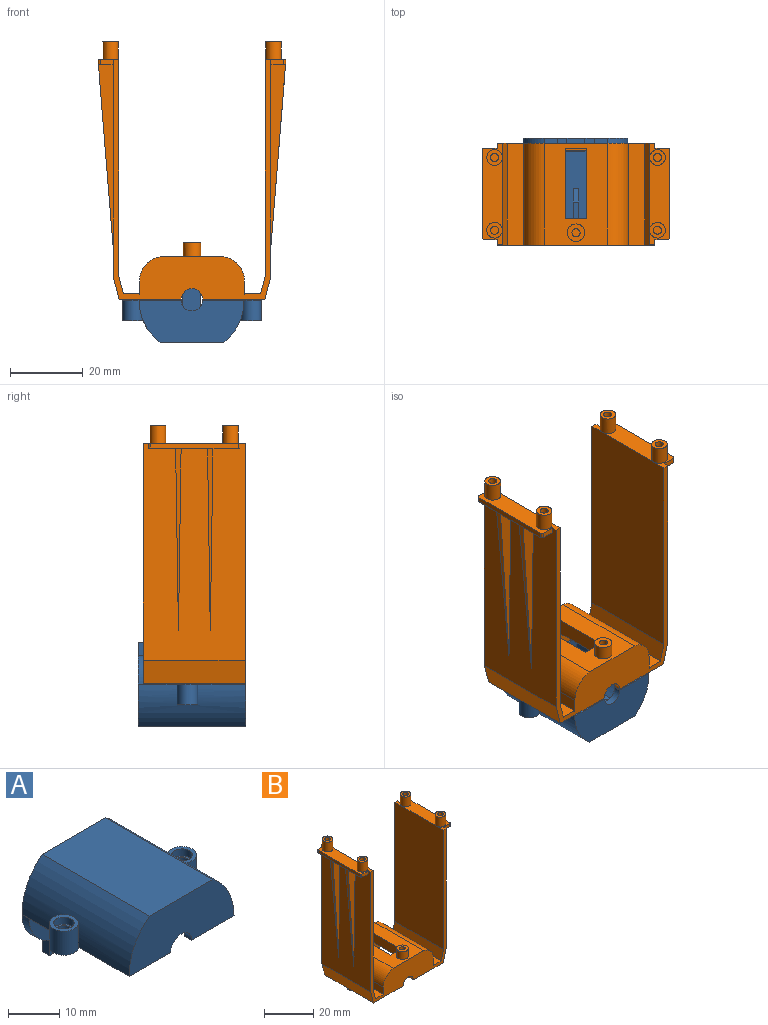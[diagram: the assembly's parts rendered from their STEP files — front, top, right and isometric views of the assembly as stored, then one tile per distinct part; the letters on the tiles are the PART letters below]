
ASSEMBLY  parts=2 mates=1
PART A: 76 faces, bbox 38.1x29.5x23.1 mm
  f0: plane 3.71x2mm, normal (-1,0,0), area 7.4mm2, adj f1,f3,f4,f74
  f1: plane 3.69x2mm, normal (0,0,-1), area 7.4mm2, adj f0,f3,f4,f60
  f2: cylinder r=14.66mm len=2mm, axis (0,1,0), area 0mm2, adj f4,f6,f13,f73
  f3: plane 11.58x9.24mm, normal (0,-1,0), area 74.7mm2, adj f0,f1,f10,f11,f60,f74
  f4: plane 28.86x23.15mm, normal (0,1,0), area 453.5mm2, adj f0,f1,f2,f6,f7,f11,f12,f14
  f5: plane 5.97x4.94mm, normal (0,-1,0), area 25mm2, adj f14,f61,f62,f72
  f6: plane 3.67x2mm, normal (0,0,-1), area 7.3mm2, adj f2,f4,f13,f63
  f7: plane 4.94x2mm, normal (0,0,-1), area 9.9mm2, adj f4,f9,f61,f62
  f8: plane 9.57x7.24mm, normal (0,-1,0), area 57.2mm2, adj f10,f14,f30,f60
  f9: plane 16.48x4.94mm, normal (0,-1,0), area 79.5mm2, adj f7,f61,f62,f72
  f10: plane 27.5x16.13mm, normal (0,0,-1), area 94.6mm2, adj f3,f8,f20,f23,f25,f28,f29,f30
  f11: cylinder r=14.66mm len=2mm, axis (0,1,0), area 0.1mm2, adj f3,f4,f28,f74
  f12: cylinder r=14.66mm len=2mm, axis (0,1,0), area 0.1mm2, adj f4,f13,f15,f75
  f13: plane 11.58x9.5mm, normal (0,-1,0), area 76.2mm2, adj f2,f6,f12,f26,f63,f73,f75
  f14: plane 27.5x16.11mm, normal (0,0,-1), area 316.2mm2, adj f4,f5,f8,f16,f18,f19,f20,f30
  f15: cylinder r=14.23mm len=29.5mm, axis (0,-1,0), area 375.1mm2, adj f4,f12,f26,f27,f29,f35
  f16: cylinder r=12.23mm len=24mm, axis (0,-1,0), area 252.2mm2, adj f14,f20,f26,f31,f55,f56,f57
  f17: plane 10x1.5mm, normal (0,0,-1), area 15mm2, adj f18,f19,f20,f46
  f18: plane 13.83x2mm, normal (1,0,0), area 23.8mm2, adj f14,f17,f20,f46
  f19: plane 13.83x2mm, normal (-1,0,0), area 23.8mm2, adj f14,f17,f20,f46
  f20: plane 24.86x9.57mm, normal (0,1,0), area 196.4mm2, adj f10,f14,f16,f17,f18,f19,f26,f30
  f21: cylinder r=14.23mm len=0.96mm, axis (0,-1,0), area 0.2mm2, adj f22,f42
  f22: cylinder r=2mm len=4mm, axis (0,0,-1), area 22.4mm2, adj f21,f37,f42,f44
  f23: cylinder r=2mm len=5.71mm, axis (0,0,-1), area 47.2mm2, adj f10,f25,f34,f38,f40,f41
  f24: cylinder r=14.23mm len=2.18mm, axis (0,-1,0), area 4.1mm2, adj f26,f36,f45
  f25: cylinder r=14.23mm len=1.62mm, axis (0,-1,0), area 1.3mm2, adj f10,f23
  f26: plane 27.5x16.13mm, normal (0,0,-1), area 94.8mm2, adj f13,f15,f16,f20,f24,f29,f31,f32
  f27: plane 29.5x17.5mm, normal (0,0,1), area 516.2mm2, adj f4,f15,f28,f29
  f28: cylinder r=14.23mm len=29.5mm, axis (0,-1,0), area 374.9mm2, adj f4,f10,f11,f27,f29,f33
  f29: plane 28.86x11.57mm, normal (0,-1,0), area 281.5mm2, adj f10,f15,f26,f27,f28,f32
  f30: cylinder r=12.23mm len=24mm, axis (0,-1,0), area 249.7mm2, adj f8,f10,f14,f20,f48,f49,f50
  f31: plane 9.57x7.5mm, normal (0,-1,0), area 58.8mm2, adj f14,f16,f26,f63
  f32: cylinder r=2.93mm len=5.86mm, axis (0,-1,0), area 18.4mm2, adj f10,f20,f26,f29
  f33: cylinder r=2.82mm len=5.71mm, axis (0,0,-1), area 82.1mm2, adj f10,f28,f34
  f34: plane 5.64x5.64mm, normal (0,0,1), area 12.4mm2, adj f23,f33
  f35: cylinder r=2.82mm len=5.71mm, axis (0,0,-1), area 77.7mm2, adj f15,f26,f37
  f36: cylinder r=2mm len=4mm, axis (0,0,-1), area 20.8mm2, adj f24,f26,f45
  f37: plane 5.64x5.64mm, normal (0,0,1), area 12.4mm2, adj f22,f35
  f38: plane 2x0.96mm, normal (1,0,0), area 1.9mm2, adj f23,f40,f41
  f39: cylinder r=1.5mm len=3mm, axis (0,0,-1), area 18.8mm2, adj f40,f41
  f40: plane 4x3.94mm, normal (0,0,1), area 5.5mm2, adj f23,f38,f39
  f41: plane 4x3.94mm, normal (0,0,-1), area 5.5mm2, adj f23,f38,f39
  f42: plane 1.18x0.96mm, normal (-1,0,0), area 1.1mm2, adj f21,f22,f44
  f43: cylinder r=1.5mm len=3mm, axis (0,0,-1), area 18.8mm2, adj f44,f45
  f44: plane 4x3.94mm, normal (0,0,1), area 5.5mm2, adj f22,f42,f43
  f45: plane 4x3.81mm, normal (0,0,-1), area 5.3mm2, adj f24,f36,f43
  f46: plane 3.83x2mm, normal (0,0.46,-0.89), area 6.5mm2, adj f14,f17,f18,f19
  f47: plane 2x1.5mm, normal (1,0,0), area 3mm2, adj f48,f49,f50,f53
  f48: plane 3.66x1.5mm, normal (0,0,-1), area 5.5mm2, adj f30,f47,f49,f50
  f49: plane 6.41x5.5mm, normal (0,-1,0), area 18.1mm2, adj f14,f30,f47,f48,f51,f52,f53
  f50: plane 6.41x5.5mm, normal (0,1,0), area 18.1mm2, adj f14,f30,f47,f48,f51,f52,f53
  f51: plane 2x1.5mm, normal (1,0,0), area 3mm2, adj f14,f49,f50,f52
  f52: plane 1.5x1.25mm, normal (0,0,-1), area 1.9mm2, adj f49,f50,f51,f53
  f53: cylinder r=1.5mm len=1.5mm, axis (0,-1,0), area 3.5mm2, adj f47,f49,f50,f52
  f54: plane 3.5x1.5mm, normal (-1,0,0), area 5.3mm2, adj f55,f56,f57,f59
  f55: plane 3.86x1.5mm, normal (0,0,-1), area 5.8mm2, adj f16,f54,f56,f57
  f56: plane 6.61x5.5mm, normal (0,-1,0), area 18.3mm2, adj f14,f16,f54,f55,f58,f59
  f57: plane 6.61x5.5mm, normal (0,1,0), area 18.3mm2, adj f14,f16,f54,f55,f58,f59
  f58: plane 2x1.5mm, normal (-1,0,0), area 3mm2, adj f14,f56,f57,f59
  f59: plane 2.75x1.5mm, normal (0,0,-1), area 4.1mm2, adj f54,f56,f57,f58
  f60: plane 21.15x3.5mm, normal (1,0,0), area 56.6mm2, adj f1,f3,f4,f8,f10,f14
  f61: plane 21.15x3.5mm, normal (-1,0,0), area 51.2mm2, adj f4,f5,f7,f9,f14,f72
  f62: plane 21.15x3.5mm, normal (1,0,0), area 51.2mm2, adj f4,f5,f7,f9,f14,f72
  f63: plane 21.15x3.5mm, normal (-1,0,0), area 56.6mm2, adj f4,f6,f13,f14,f26,f31
  f64: cylinder r=2.17mm len=4.35mm, axis (0,0,1), area 6.8mm2, adj f14,f65
  f65: plane 4.35x4.35mm, normal (0,0,-1), area 14.9mm2, adj f64
  f66: cylinder r=2.17mm len=4.35mm, axis (0,0,1), area 6.8mm2, adj f14,f67
  f67: plane 4.35x4.35mm, normal (0,0,-1), area 14.9mm2, adj f66
  f68: cylinder r=2.17mm len=4.35mm, axis (0,0,1), area 6.8mm2, adj f14,f69
  f69: plane 4.35x4.35mm, normal (0,0,-1), area 14.9mm2, adj f68
  f70: cylinder r=2.17mm len=4.35mm, axis (0,0,1), area 6.8mm2, adj f14,f71
  f71: plane 4.35x4.35mm, normal (0,0,-1), area 14.9mm2, adj f70
  f72: cylinder r=3mm len=4.94mm, axis (0,-1,0), area 8.7mm2, adj f5,f9,f61,f62
  f73: plane 3.69x2mm, normal (1,0,0), area 7.4mm2, adj f2,f4,f13,f75
  f74: cylinder r=8.25mm len=7.82mm, axis (0,-1,0), area 20.5mm2, adj f0,f3,f4,f11
  f75: cylinder r=8.3mm len=7.82mm, axis (0,-1,0), area 20.8mm2, adj f4,f12,f13,f73
PART B: 131 faces, bbox 51.5x28x73.1 mm
  f0: plane 7.28x4.03mm, normal (0,0,-1), area 29.3mm2, adj f4,f6,f25,f102
  f1: plane 7.41x4.02mm, normal (0,0,-1), area 29.7mm2, adj f2,f5,f25,f66,f102
  f2: cylinder r=0.5mm len=1.5mm, axis (0,0,1), area 1.2mm2, adj f1,f3,f23,f66,f102
  f3: plane 24.1x1.5mm, normal (-1,0,0), area 33.9mm2, adj f2,f23,f24,f67,f102
  f4: plane 49.87x4.02mm, normal (0,-1,-0.01), area 100.2mm2, adj f0,f25,f102
  f5: plane 49.87x4.02mm, normal (0,1,-0.02), area 100.2mm2, adj f1,f25,f102
  f6: plane 50x4.03mm, normal (0,1,-0.01), area 100.7mm2, adj f0,f25,f102
  f7: plane 50x4.03mm, normal (0,1,-0.02), area 100.8mm2, adj f19,f22,f101
  f8: plane 7.41x4.02mm, normal (0,0,-1), area 29.7mm2, adj f11,f13,f19,f71,f101
  f9: plane 7.28x4.03mm, normal (0,0,-1), area 29.3mm2, adj f12,f14,f19,f101
  f10: plane 24.1x1.5mm, normal (1,0,0), area 33.9mm2, adj f11,f22,f47,f70,f101
  f11: cylinder r=0.5mm len=1.5mm, axis (0,0,1), area 1.2mm2, adj f8,f10,f47,f71,f101
  f12: plane 50x4.03mm, normal (0,-1,-0.01), area 100.7mm2, adj f9,f19,f101
  f13: plane 49.86x4.02mm, normal (0,-1,-0.01), area 100.2mm2, adj f8,f19,f101
  f14: plane 49.86x4.02mm, normal (0,1,-0.01), area 100.2mm2, adj f9,f19,f101
  f15: plane 24.86x9.68mm, normal (0,1,0), area 204.8mm2, adj f17,f28,f30,f35,f36,f37,f38,f39
  f16: plane 24.86x9.68mm, normal (0,-1,0), area 181.8mm2, adj f18,f28,f30,f35,f36,f37,f38,f39
  f17: plane 13.2x4.07mm, normal (0,0,-1), area 53.8mm2, adj f15,f35,f94,f97
  f18: plane 9.3x4.07mm, normal (0,0,-1), area 37.9mm2, adj f16,f35,f94,f96
  f19: plane 59.6x28mm, normal (1,0,0), area 1556.2mm2, adj f7,f8,f9,f12,f13,f14,f20,f21
  f20: plane 65.93x43.42mm, normal (0,1,0), area 505.3mm2, adj f19,f23,f25,f26,f27,f28,f29,f30
  f21: plane 65.93x43.42mm, normal (0,-1,0), area 516.2mm2, adj f19,f23,f25,f26,f27,f28,f29,f30
  f22: plane 7.41x4.03mm, normal (0,0,-1), area 29.8mm2, adj f7,f10,f19,f69,f70
  f23: plane 28x5.53mm, normal (0,0,1), area 113.9mm2, adj f2,f3,f20,f21,f25,f54,f66,f67
  f24: plane 7.41x4.03mm, normal (0,0,-1), area 29.8mm2, adj f3,f25,f67,f68,f88
  f25: plane 59.6x28mm, normal (-1,0,0), area 1556.2mm2, adj f0,f1,f4,f5,f6,f20,f21,f23
  f26: plane 28x17.5mm, normal (0,0,1), area 357.3mm2, adj f20,f21,f31,f32,f58,f62,f63,f64
  f27: plane 28x0.02mm, normal (0,0,1), area 0.5mm2, adj f20,f21,f33,f53
  f28: plane 28x17.09mm, normal (0,0,-1), area 205mm2, adj f15,f16,f20,f21,f40,f52,f118,f121
  f29: plane 28x0.02mm, normal (0,0,1), area 0.5mm2, adj f20,f21,f34,f51
  f30: plane 28x17.09mm, normal (0,0,-1), area 205mm2, adj f15,f16,f20,f21,f40,f46,f114,f125
  f31: cylinder r=6.77mm len=28mm, axis (0,-1,0), area 267.1mm2, adj f20,f21,f26,f34
  f32: cylinder r=6.77mm len=28mm, axis (0,-1,0), area 267.1mm2, adj f20,f21,f26,f33
  f33: plane 28x3.65mm, normal (-1,0,0), area 102.2mm2, adj f20,f21,f27,f32
  f34: plane 28x3.65mm, normal (1,0,0), area 102.2mm2, adj f20,f21,f29,f31
  f35: cylinder r=4.77mm len=24mm, axis (0,-1,0), area 150.3mm2, adj f15,f16,f17,f18,f39,f96,f97,f98
  f36: plane 24x4.07mm, normal (0,0,-1), area 97.8mm2, adj f15,f16,f37,f92
  f37: cylinder r=4.77mm len=24mm, axis (0,-1,0), area 150.3mm2, adj f15,f16,f36,f38,f107,f108,f110,f112
  f38: plane 24x6.5mm, normal (1,0,0), area 156mm2, adj f15,f16,f37,f121,f123,f124
  f39: plane 24x6.5mm, normal (-1,0,0), area 156mm2, adj f15,f16,f35,f125,f127,f128
  f40: cylinder r=2.93mm len=5.86mm, axis (0,-1,0), area 18.4mm2, adj f15,f21,f28,f30
  f41: plane 2x0.19mm, normal (-0.59,0,-0.81), area 0.5mm2, adj f16,f20,f45,f129
  f42: plane 2x0.19mm, normal (0.59,0,-0.81), area 0.5mm2, adj f16,f20,f43,f130
  f43: cylinder r=1mm len=2mm, axis (0,1,0), area 1.3mm2, adj f16,f20,f42,f44
  f44: plane 4.75x2mm, normal (0,0,-1), area 9.5mm2, adj f16,f20,f43,f45
  f45: cylinder r=1mm len=2mm, axis (0,1,0), area 1.3mm2, adj f16,f20,f41,f44
  f46: plane 28x6.33mm, normal (0.97,0,-0.26), area 183.4mm2, adj f19,f20,f21,f30
  f47: plane 28x5.53mm, normal (0,0,1), area 113.9mm2, adj f10,f11,f19,f20,f21,f48,f69,f70
  f48: plane 59.4x28mm, normal (-1,0,0), area 1663.3mm2, adj f20,f21,f47,f49
  f49: plane 28x5.03mm, normal (-0.97,0,0.26), area 145.6mm2, adj f20,f21,f48,f50
  f50: plane 28x4.42mm, normal (0,0,1), area 123.7mm2, adj f20,f21,f49,f51
  f51: plane 28x0.15mm, normal (-1,0,0), area 4.2mm2, adj f20,f21,f29,f50
  f52: plane 28x6.33mm, normal (-0.97,0,-0.26), area 183.4mm2, adj f20,f21,f25,f28
  f53: plane 28x0.15mm, normal (1,0,0), area 4.2mm2, adj f20,f21,f27,f55
  f54: plane 59.4x28mm, normal (1,0,0), area 1663.3mm2, adj f20,f21,f23,f56
  f55: plane 28x4.42mm, normal (0,0,1), area 123.7mm2, adj f20,f21,f53,f56
  f56: plane 28x5.03mm, normal (0.97,0,0.26), area 145.6mm2, adj f20,f21,f54,f55
  f57: cylinder r=1.11mm len=3.8mm, axis (0,0,-1), area 26.5mm2, adj f59,f60
  f58: cylinder r=2.4mm len=4.8mm, axis (0,0,-1), area 57.3mm2, adj f26,f59
  f59: plane 4.8x4.8mm, normal (0,0,1), area 14.2mm2, adj f57,f58
  f60: plane 2.22x2.22mm, normal (0,0,1), area 3.9mm2, adj f57
  f61: plane 6x0.5mm, normal (0,0,1), area 3mm2, adj f16,f62,f63,f64
  f62: plane 24.5x5mm, normal (1,0,0), area 96.6mm2, adj f15,f16,f26,f61,f64,f65,f93,f99
  f63: plane 24.5x5mm, normal (-1,0,0), area 96.6mm2, adj f15,f16,f26,f61,f64,f65,f95,f100
  f64: plane 6x5mm, normal (0,-1,0), area 30mm2, adj f26,f61,f62,f63
  f65: plane 6x4.48mm, normal (0,1,0), area 17.9mm2, adj f26,f62,f63,f89,f90,f91,f99,f100
  f66: plane 3.53x1.5mm, normal (0,1,0), area 5.3mm2, adj f1,f2,f23,f25
  f67: cylinder r=0.5mm len=1.5mm, axis (0,0,1), area 1.2mm2, adj f3,f23,f24,f68
  f68: plane 3.53x1.5mm, normal (0,-1,0), area 5.3mm2, adj f23,f24,f25,f67
  f69: plane 3.53x1.5mm, normal (0,1,0), area 5.3mm2, adj f19,f22,f47,f70
  f70: cylinder r=0.5mm len=1.5mm, axis (0,0,1), area 1.2mm2, adj f10,f22,f47,f69
  f71: plane 3.53x1.5mm, normal (0,-1,0), area 5.3mm2, adj f8,f11,f19,f47
  f72: cylinder r=1.11mm len=4.9mm, axis (0,0,-1), area 34.2mm2, adj f74,f75
  f73: cylinder r=2.15mm len=4.9mm, axis (0,0,-1), area 66.3mm2, adj f23,f74
  f74: plane 4.31x4.31mm, normal (0,0,1), area 10.7mm2, adj f72,f73
  f75: plane 2.22x2.22mm, normal (0,0,1), area 3.9mm2, adj f72
  f76: cylinder r=2.15mm len=4.9mm, axis (0,0,-1), area 66.3mm2, adj f23,f78
  f77: cylinder r=1.11mm len=4.9mm, axis (0,0,-1), area 34.2mm2, adj f78,f79
  f78: plane 4.31x4.31mm, normal (0,0,1), area 10.7mm2, adj f76,f77
  f79: plane 2.22x2.22mm, normal (0,0,1), area 3.9mm2, adj f77
  f80: cylinder r=1.11mm len=4.9mm, axis (0,0,-1), area 34.2mm2, adj f82,f83
  f81: cylinder r=2.15mm len=4.9mm, axis (0,0,-1), area 66.3mm2, adj f47,f82
  f82: plane 4.31x4.31mm, normal (0,0,1), area 10.7mm2, adj f80,f81
  f83: plane 2.22x2.22mm, normal (0,0,1), area 3.9mm2, adj f80
  f84: cylinder r=2.15mm len=4.9mm, axis (0,0,-1), area 66.3mm2, adj f47,f86
  f85: cylinder r=1.11mm len=4.9mm, axis (0,0,-1), area 34.2mm2, adj f86,f87
  f86: plane 4.31x4.31mm, normal (0,0,1), area 10.7mm2, adj f84,f85
  f87: plane 2.22x2.22mm, normal (0,0,1), area 3.9mm2, adj f85
  f88: plane 50x4.03mm, normal (0,-1,-0.01), area 100.8mm2, adj f24,f25,f102
  f89: plane 5.4x2mm, normal (-1,0,0), area 10.8mm2, adj f15,f65,f91,f99
  f90: plane 5.4x2mm, normal (1,0,0), area 10.8mm2, adj f15,f65,f91,f100
  f91: plane 5.4x1.5mm, normal (0,0,-1), area 8.1mm2, adj f15,f65,f89,f90
  f92: plane 24x2.48mm, normal (-1,0,0), area 57.3mm2, adj f15,f16,f36,f93,f107,f108,f109,f110
  f93: plane 24x1.5mm, normal (0,0,-1), area 36mm2, adj f15,f16,f62,f92
  f94: plane 24x2.48mm, normal (1,0,0), area 56.5mm2, adj f15,f16,f17,f18,f95,f96,f97,f105
  f95: plane 24x1.5mm, normal (0,0,-1), area 36mm2, adj f15,f16,f63,f94
  f96: plane 7.93x4.48mm, normal (0,1,0), area 25.7mm2, adj f18,f35,f94,f98,f103,f104,f105,f106
  f97: plane 7.93x4.48mm, normal (0,-1,0), area 25.7mm2, adj f17,f35,f94,f98,f103,f104,f105,f106
  f98: plane 1.5x0.48mm, normal (1,0,0), area 0.7mm2, adj f35,f96,f97,f103
  f99: plane 5.4x2.25mm, normal (0,0,-1), area 12.1mm2, adj f15,f62,f65,f89
  f100: plane 5.4x2.25mm, normal (0,0,-1), area 12.1mm2, adj f15,f63,f65,f90
  f101: plane 50.27x17.34mm, normal (1,0,-0.08), area 77.6mm2, adj f7,f8,f9,f10,f11,f12,f13,f14
  f102: plane 50.26x17.33mm, normal (-1,0,-0.08), area 77.5mm2, adj f0,f1,f2,f3,f4,f5,f6,f25
  f103: plane 1.5x1.32mm, normal (0,0,1), area 2mm2, adj f35,f96,f97,f98
  f104: plane 5.93x1.5mm, normal (0,0,-1), area 8.9mm2, adj f35,f96,f97,f106
  f105: plane 2x1.5mm, normal (0,0,-1), area 3mm2, adj f94,f96,f97,f106
  f106: plane 2.5x1.5mm, normal (-1,0,0), area 3.8mm2, adj f96,f97,f104,f105
  f107: plane 7.93x4mm, normal (0,-1,0), area 23.7mm2, adj f37,f92,f109,f110,f111,f112
  f108: plane 7.93x4mm, normal (0,1,0), area 23.7mm2, adj f37,f92,f109,f110,f111,f112
  f109: plane 2x1.5mm, normal (0,0,-1), area 3mm2, adj f92,f107,f108,f111
  f110: plane 5.42x1.5mm, normal (0,0,1), area 8.1mm2, adj f37,f92,f107,f108
  f111: plane 2.5x1.5mm, normal (1,0,0), area 3.8mm2, adj f107,f108,f109,f112
  f112: plane 5.93x1.5mm, normal (0,0,-1), area 8.9mm2, adj f37,f107,f108,f111
  f113: cylinder r=1.1mm len=2.29mm, axis (0,0,1), area 15.9mm2, adj f115,f116
  f114: cylinder r=2.15mm len=4.3mm, axis (0,0,1), area 30.9mm2, adj f30,f115
  f115: plane 4.3x4.3mm, normal (0,0,-1), area 10.7mm2, adj f113,f114
  f116: plane 2.21x2.21mm, normal (0,0,-1), area 3.8mm2, adj f113
  f117: cylinder r=1.1mm len=2.29mm, axis (0,0,1), area 15.9mm2, adj f119,f120
  f118: cylinder r=2.15mm len=4.3mm, axis (0,0,1), area 30.9mm2, adj f28,f119
  f119: plane 4.3x4.3mm, normal (0,0,-1), area 10.7mm2, adj f117,f118
  f120: plane 2.21x2.21mm, normal (0,0,-1), area 3.8mm2, adj f117
  f121: plane 1.5x1.14mm, normal (0,-1,0), area 1.7mm2, adj f28,f38,f122,f124
  f122: plane 24x1.5mm, normal (-1,0,0), area 36mm2, adj f28,f121,f123,f124
  f123: plane 1.5x1.14mm, normal (0,1,0), area 1.7mm2, adj f28,f38,f122,f124
  f124: plane 24x1.14mm, normal (0,0,-1), area 27.4mm2, adj f38,f121,f122,f123
  f125: plane 1.5x1.14mm, normal (0,1,0), area 1.7mm2, adj f30,f39,f126,f128
  f126: plane 24x1.5mm, normal (1,0,0), area 36mm2, adj f30,f125,f127,f128
  f127: plane 1.5x1.14mm, normal (0,-1,0), area 1.7mm2, adj f30,f39,f126,f128
  f128: plane 24x1.14mm, normal (0,0,-1), area 27.4mm2, adj f39,f125,f126,f127
  f129: cylinder r=4mm len=2.67mm, axis (0,-1,0), area 6.4mm2, adj f16,f20,f30,f41
  f130: cylinder r=4mm len=2.67mm, axis (0,-1,0), area 6.4mm2, adj f16,f20,f28,f42
PLACE A rot(axis=(0,1,0),180deg) t=(-0.74,-14.22,-33.88)mm
PLACE B t=(-0.73,-0.11,-33.59)mm
MATE fastened A.f23 <-> B.f113  axis (0,0,1) through (15.5,1.78,-35.88)mm
